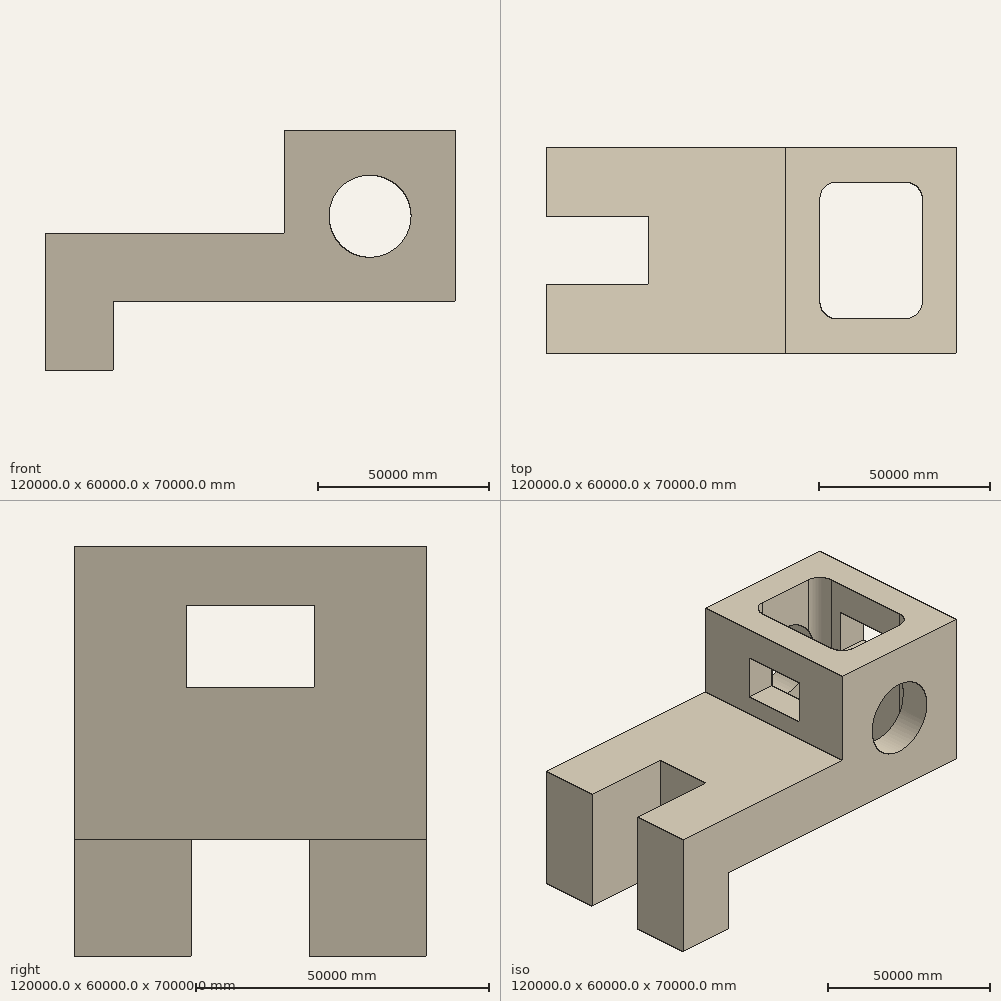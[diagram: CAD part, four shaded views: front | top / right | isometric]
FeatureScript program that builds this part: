
annotation { "Feature Type Name" : "Feature", "Feature Type Description" : "" }
export const myFeature = defineFeature(function(context is Context, id is Id, definition is map)
    precondition{}
    {
        {
            var Q0;
            Q0=qCreatedBy(makeId("Front.planeOp"),FACE);
            var sketch = newSketch(context, id + "F0", { "sketchPlane" : qUnion([Q0])});
            skLineSegment(sketch, "E0.bottom", {"start": v(-25000, -25000) * mm, "end": v(25000, -25000) * mm});
            skLineSegment(sketch, "E0.top", {"start": v(-25000, 25000) * mm, "end": v(25000, 25000) * mm});
            skLineSegment(sketch, "E0.left", {"start": v(-25000, -5000) * mm, "end": v(-25000, 25000) * mm});
            skLineSegment(sketch, "E0.right", {"start": v(25000, -25000) * mm, "end": v(25000, 25000) * mm});
            skPoint(sketch, "E0.middle", {"position": v(0, 0) * mm});
            skLineSegment(sketch, "E1.bottom", {"start": v(-25000, -25000) * mm, "end": v(-75000, -25000) * mm});
            skLineSegment(sketch, "E1.top", {"start": v(-25000, -5000) * mm, "end": v(-95000, -5000) * mm});
            skLineSegment(sketch, "E1.right", {"start": v(-95000, -25000) * mm, "end": v(-95000, -5000) * mm});
            skLineSegment(sketch, "E2.top", {"start": v(-95000, -45000) * mm, "end": v(-75000, -45000) * mm});
            skLineSegment(sketch, "E2.left", {"start": v(-95000, -25000) * mm, "end": v(-95000, -45000) * mm});
            skLineSegment(sketch, "E2.right", {"start": v(-75000, -25000) * mm, "end": v(-75000, -45000) * mm});
            skSolve(sketch);
        }
        {
            var Q0;
            Q0 = qSketchRegion(id + "F0", true);
            extrude(context, id + "F1", {"entities" : qUnion([Q0]), "depth" : 60000 * mm, "offsetDistance" : 25 * mm});
        }
        {
            var Q0;
            Q0=makeQuery(id+"F1.opExtrude","CAP_FACE",FACE,{"disambiguationData":[OSD([sQuery(id+"F0.wireOp",EDGE,"E0.bottom"),sQuery(id+"F0.wireOp",EDGE,"E0.top"),sQuery(id+"F0.wireOp",EDGE,"E0.left"),sQuery(id+"F0.wireOp",EDGE,"E0.right"),sQuery(id+"F0.wireOp",EDGE,"E1.bottom"),sQuery(id+"F0.wireOp",EDGE,"E1.top"),sQuery(id+"F0.wireOp",EDGE,"E1.right"),sQuery(id+"F0.wireOp",EDGE,"E2.top"),sQuery(id+"F0.wireOp",EDGE,"E2.left"),sQuery(id+"F0.wireOp",EDGE,"E2.right")])],"isStart":false});
            var sketch = newSketch(context, id + "F2", { "sketchPlane" : qUnion([Q0])});
            skCircle(sketch, "E3", {"center": v(0, 0) * mm, "radius": 12000 * mm});
            skSolve(sketch);
        }
        {
            var Q0;
            Q0 = qSketchRegion(id + "F2", true);
            extrude(context, id + "F3", {"entities" : qUnion([Q0]), "operationType" : NewBodyOperationType.REMOVE, "endBound" : BoundingType.THROUGH_ALL, "oppositeDirection" : true, "depth" : 25 * mm, "offsetDistance" : 25 * mm});
        }
        {
            var Q0;
            Q0=makeQuery(id+"F1.opExtrude","SWEPT_FACE",FACE,{"disambiguationData":[OSD([sQuery(id+"F0.wireOp",EDGE,"E0.top")])]});
            var sketch = newSketch(context, id + "F4", { "sketchPlane" : qUnion([Q0])});
            skLineSegment(sketch, "E4.bottom", {"start": v(-10000, -50000) * mm, "end": v(10000, -50000) * mm});
            skLineSegment(sketch, "E4.top", {"start": v(-10000, -10000) * mm, "end": v(10000, -10000) * mm});
            skLineSegment(sketch, "E4.left", {"start": v(-15000, -45000) * mm, "end": v(-15000, -15000) * mm});
            skLineSegment(sketch, "E4.right", {"start": v(15000, -45000) * mm, "end": v(15000, -15000) * mm});
            skPoint(sketch, "E4.middle", {"position": v(0, -30000) * mm});
            skPoint(sketch, "E4.middle.positionSnap0", {"position": v(25000, -30000) * mm});
            skPoint(sketch, "E4.middle.positionSnap1", {"position": v(0, 0) * mm});
            skPoint(sketch, "E4.centerSnap0", {"position": v(25000, -30000) * mm});
            skPoint(sketch, "E4.centerSnap1", {"position": v(0, 0) * mm});
            skPoint(sketch, "E5.visualSharp", {"position": v(-15000, -10000) * mm});
            skArc(sketch, "E5.filletArc", {"start": v(-10000, -10000) * mm, "mid": v(-13535.53, -11464.47) * mm, "end": v(-15000, -15000) * mm});
            skPoint(sketch, "E6.visualSharp", {"position": v(15000, -10000) * mm});
            skArc(sketch, "E6.filletArc", {"start": v(15000, -15000) * mm, "mid": v(13535.53, -11464.47) * mm, "end": v(10000, -10000) * mm});
            skPoint(sketch, "E7.visualSharp", {"position": v(15000, -50000) * mm});
            skArc(sketch, "E7.filletArc", {"start": v(10000, -50000) * mm, "mid": v(13535.53, -48535.53) * mm, "end": v(15000, -45000) * mm});
            skPoint(sketch, "E8.visualSharp", {"position": v(-15000, -50000) * mm});
            skArc(sketch, "E8.filletArc", {"start": v(-15000, -45000) * mm, "mid": v(-13535.53, -48535.53) * mm, "end": v(-10000, -50000) * mm});
            skSolve(sketch);
        }
        {
            var Q0;
            Q0 = qSketchRegion(id + "F4", true);
            extrude(context, id + "F5", {"entities" : qUnion([Q0]), "operationType" : NewBodyOperationType.REMOVE, "endBound" : BoundingType.THROUGH_ALL, "oppositeDirection" : true, "depth" : 25 * mm, "offsetDistance" : 25 * mm});
        }
        {
            var Q0;
            Q0=makeQuery(id+"F1.opExtrude","SWEPT_FACE",FACE,{"disambiguationData":[OSD([sQuery(id+"F0.wireOp",EDGE,"E0.right")])]});
            var sketch = newSketch(context, id + "F6", { "sketchPlane" : qUnion([Q0])});
            skLineSegment(sketch, "E9.bottom", {"start": v(-41000, 1000) * mm, "end": v(-19000, 1000) * mm});
            skLineSegment(sketch, "E9.top", {"start": v(-41000, 15000) * mm, "end": v(-19000, 15000) * mm});
            skLineSegment(sketch, "E9.left", {"start": v(-41000, 1000) * mm, "end": v(-41000, 15000) * mm});
            skLineSegment(sketch, "E9.right", {"start": v(-19000, 1000) * mm, "end": v(-19000, 15000) * mm});
            skPoint(sketch, "E9.middle", {"position": v(-30000, 8000) * mm});
            skPoint(sketch, "E9.middle.positionSnap0", {"position": v(-30000, 25000) * mm});
            skPoint(sketch, "E9.centerSnap0", {"position": v(-30000, 25000) * mm});
            skSolve(sketch);
        }
        {
            var Q0;
            Q0 = qSketchRegion(id + "F6", true);
            extrude(context, id + "F7", {"entities" : qUnion([Q0]), "operationType" : NewBodyOperationType.REMOVE, "endBound" : BoundingType.THROUGH_ALL, "oppositeDirection" : true, "depth" : 25 * mm, "offsetDistance" : 25 * mm});
        }
        {
            var Q0;
            Q0=makeQuery(id+"F1.opExtrude","SWEPT_FACE",FACE,{"disambiguationData":[OSD([sQuery(id+"F0.wireOp",EDGE,"E1.top")])]});
            var sketch = newSketch(context, id + "F8", { "sketchPlane" : qUnion([Q0])});
            skLineSegment(sketch, "E10.bottom", {"start": v(-95000, -40000) * mm, "end": v(-65000, -40000) * mm});
            skLineSegment(sketch, "E10.top", {"start": v(-95000, -20000) * mm, "end": v(-65000, -20000) * mm});
            skLineSegment(sketch, "E10.left", {"start": v(-95000, -40000) * mm, "end": v(-95000, -20000) * mm});
            skLineSegment(sketch, "E10.right", {"start": v(-65000, -40000) * mm, "end": v(-65000, -20000) * mm});
            skPoint(sketch, "E10.middle", {"position": v(-80000, -30000) * mm});
            skPoint(sketch, "E10.middle.positionSnap0", {"position": v(-95000, -30000) * mm});
            skPoint(sketch, "E10.centerSnap0", {"position": v(-95000, -30000) * mm});
            skSolve(sketch);
        }
        {
            var Q0;
            Q0 = qSketchRegion(id + "F8", true);
            extrude(context, id + "F9", {"entities" : qUnion([Q0]), "operationType" : NewBodyOperationType.REMOVE, "endBound" : BoundingType.THROUGH_ALL, "oppositeDirection" : true, "depth" : 25 * mm, "offsetDistance" : 25 * mm});
        }
    });
